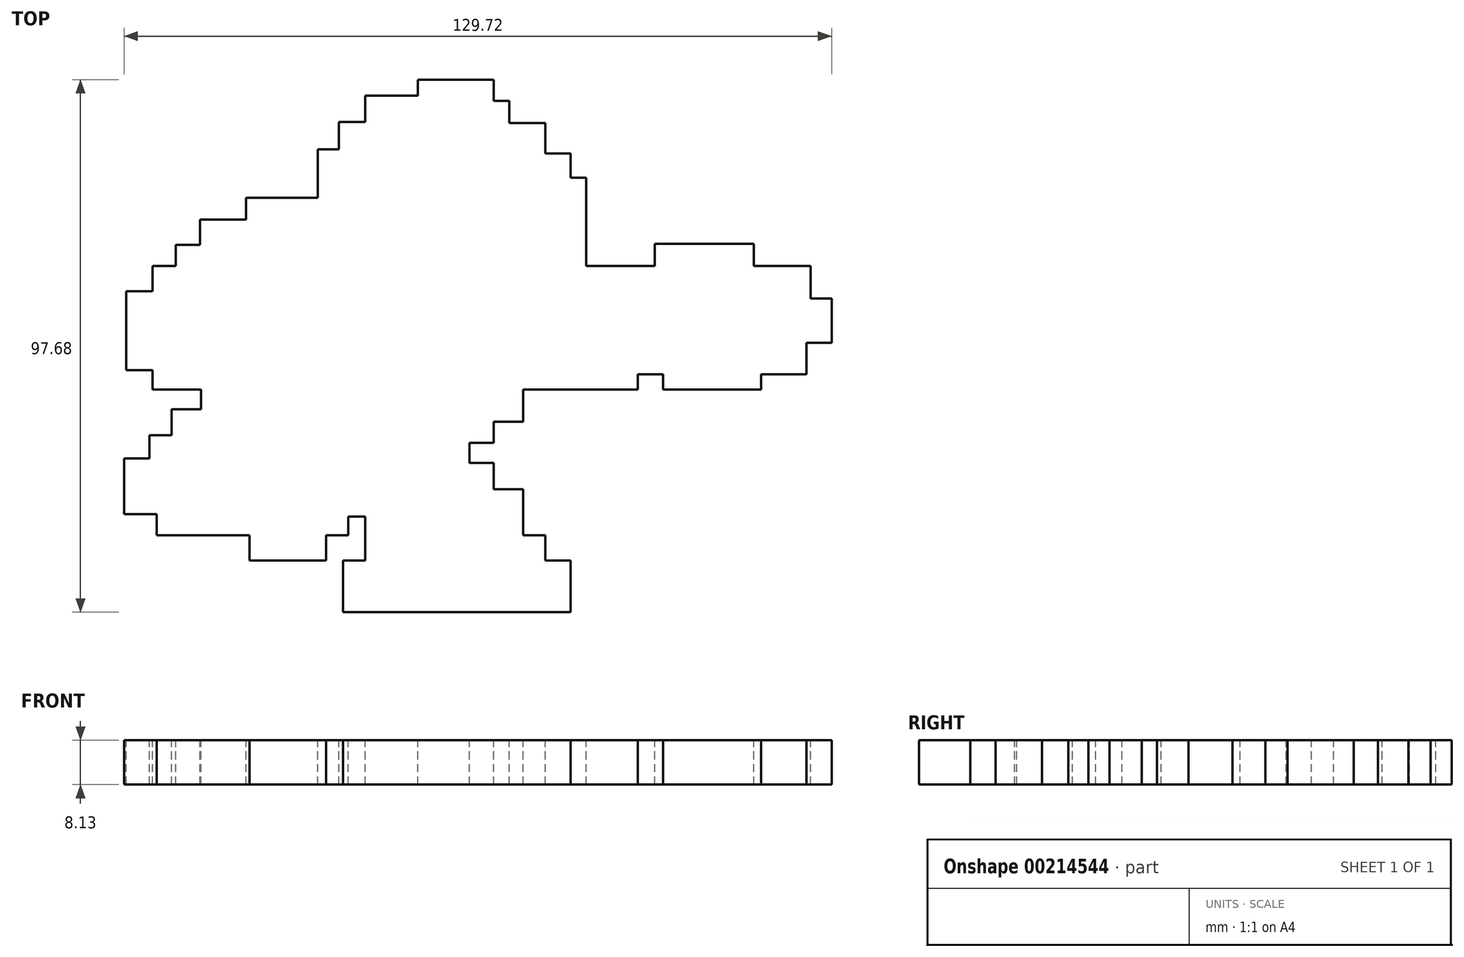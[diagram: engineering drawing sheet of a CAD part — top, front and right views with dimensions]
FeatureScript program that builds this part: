
annotation { "Feature Type Name" : "Feature", "Feature Type Description" : "" }
export const myFeature = defineFeature(function(context is Context, id is Id, definition is map)
    precondition{}
    {
        {
            var Q0;
            Q0=qCreatedBy(makeId("Top.planeOp"),FACE);
            var sketch = newSketch(context, id + "F0", { "sketchPlane" : qUnion([Q0])});
            skLineSegment(sketch, "E0", {"start": v(-13.9, 56.85) * mm, "end": v(0, 56.85) * mm});
            skLineSegment(sketch, "E1", {"start": v(0, 56.85) * mm, "end": v(0, 52.99) * mm});
            skLineSegment(sketch, "E2", {"start": v(0, 52.99) * mm, "end": v(2.9, 52.99) * mm});
            skLineSegment(sketch, "E3", {"start": v(2.9, 52.99) * mm, "end": v(2.9, 48.93) * mm});
            skLineSegment(sketch, "E4", {"start": v(2.9, 48.93) * mm, "end": v(9.47, 48.93) * mm});
            skLineSegment(sketch, "E5", {"start": v(9.47, 48.93) * mm, "end": v(9.47, 43.33) * mm});
            skLineSegment(sketch, "E6", {"start": v(9.47, 43.33) * mm, "end": v(14.1, 43.33) * mm});
            skLineSegment(sketch, "E7", {"start": v(14.1, 43.33) * mm, "end": v(14.1, 38.9) * mm});
            skLineSegment(sketch, "E8", {"start": v(14.1, 38.9) * mm, "end": v(17, 38.9) * mm});
            skLineSegment(sketch, "E9", {"start": v(17, 38.9) * mm, "end": v(17, 22.68) * mm});
            skLineSegment(sketch, "E10", {"start": v(17, 22.68) * mm, "end": v(29.54, 22.68) * mm});
            skLineSegment(sketch, "E11", {"start": v(29.54, 22.68) * mm, "end": v(29.54, 26.73) * mm});
            skLineSegment(sketch, "E12", {"start": v(29.54, 26.73) * mm, "end": v(47.69, 26.73) * mm});
            skLineSegment(sketch, "E13", {"start": v(47.69, 26.73) * mm, "end": v(47.69, 22.68) * mm});
            skLineSegment(sketch, "E14", {"start": v(47.69, 22.68) * mm, "end": v(58.1, 22.68) * mm});
            skLineSegment(sketch, "E15", {"start": v(58.1, 22.68) * mm, "end": v(58.1, 16.7) * mm});
            skLineSegment(sketch, "E16", {"start": v(58.1, 16.7) * mm, "end": v(61.97, 16.7) * mm});
            skLineSegment(sketch, "E17", {"start": v(61.97, 16.7) * mm, "end": v(61.97, 8.59) * mm});
            skLineSegment(sketch, "E18", {"start": v(61.97, 8.59) * mm, "end": v(57.34, 8.59) * mm});
            skLineSegment(sketch, "E19", {"start": v(57.34, 8.59) * mm, "end": v(57.34, 2.8) * mm});
            skLineSegment(sketch, "E20", {"start": v(57.34, 2.8) * mm, "end": v(49.04, 2.8) * mm});
            skLineSegment(sketch, "E21", {"start": v(49.04, 2.8) * mm, "end": v(49.04, 0) * mm});
            skLineSegment(sketch, "E22", {"start": v(49.04, 0) * mm, "end": v(31.09, 0) * mm});
            skLineSegment(sketch, "E23", {"start": v(31.09, 0) * mm, "end": v(31.09, 2.8) * mm});
            skLineSegment(sketch, "E24", {"start": v(31.09, 2.8) * mm, "end": v(26.45, 2.8) * mm});
            skLineSegment(sketch, "E25", {"start": v(26.45, 2.8) * mm, "end": v(26.45, 0) * mm});
            skLineSegment(sketch, "E26", {"start": v(26.45, 0) * mm, "end": v(5.41, 0) * mm});
            skLineSegment(sketch, "E27", {"start": v(5.41, 0) * mm, "end": v(5.41, -5.89) * mm});
            skLineSegment(sketch, "E28", {"start": v(5.41, -5.89) * mm, "end": v(0, -5.89) * mm});
            skLineSegment(sketch, "E29", {"start": v(0, -5.89) * mm, "end": v(0, -9.75) * mm});
            skLineSegment(sketch, "E30", {"start": v(0, -9.75) * mm, "end": v(-4.43, -9.75) * mm});
            skLineSegment(sketch, "E31", {"start": v(-4.43, -9.75) * mm, "end": v(-4.43, -13.42) * mm});
            skLineSegment(sketch, "E32", {"start": v(-4.43, -13.42) * mm, "end": v(0, -13.42) * mm});
            skLineSegment(sketch, "E33", {"start": v(0, -13.42) * mm, "end": v(0, -18.24) * mm});
            skLineSegment(sketch, "E34", {"start": v(0, -18.24) * mm, "end": v(5.41, -18.24) * mm});
            skLineSegment(sketch, "E35", {"start": v(5.41, -18.24) * mm, "end": v(5.41, -26.73) * mm});
            skLineSegment(sketch, "E36", {"start": v(5.41, -26.73) * mm, "end": v(9.47, -26.73) * mm});
            skLineSegment(sketch, "E37", {"start": v(9.47, -26.73) * mm, "end": v(9.47, -31.37) * mm});
            skLineSegment(sketch, "E38", {"start": v(9.47, -31.37) * mm, "end": v(14.1, -31.37) * mm});
            skLineSegment(sketch, "E39", {"start": v(14.1, -31.37) * mm, "end": v(14.1, -40.83) * mm});
            skLineSegment(sketch, "E40", {"start": v(14.1, -40.83) * mm, "end": v(-27.6, -40.83) * mm});
            skLineSegment(sketch, "E41", {"start": v(-27.6, -40.83) * mm, "end": v(-27.6, -31.37) * mm});
            skLineSegment(sketch, "E42", {"start": v(-27.6, -31.37) * mm, "end": v(-23.54, -31.37) * mm});
            skLineSegment(sketch, "E43", {"start": v(-23.54, -31.37) * mm, "end": v(-23.54, -23.26) * mm});
            skLineSegment(sketch, "E44", {"start": v(-23.54, -23.26) * mm, "end": v(-26.63, -23.26) * mm});
            skLineSegment(sketch, "E45", {"start": v(-26.63, -23.26) * mm, "end": v(-26.63, -26.73) * mm});
            skLineSegment(sketch, "E46", {"start": v(-26.63, -26.73) * mm, "end": v(-30.68, -26.73) * mm});
            skLineSegment(sketch, "E47", {"start": v(-30.68, -26.73) * mm, "end": v(-30.68, -31.37) * mm});
            skLineSegment(sketch, "E48", {"start": v(-30.68, -31.37) * mm, "end": v(-44.77, -31.37) * mm});
            skLineSegment(sketch, "E49", {"start": v(-44.77, -31.37) * mm, "end": v(-44.77, -26.73) * mm});
            skLineSegment(sketch, "E50", {"start": v(-44.77, -26.73) * mm, "end": v(-61.76, -26.73) * mm});
            skLineSegment(sketch, "E51", {"start": v(-61.76, -26.73) * mm, "end": v(-61.76, -22.87) * mm});
            skLineSegment(sketch, "E52", {"start": v(-61.76, -22.87) * mm, "end": v(-67.75, -22.87) * mm});
            skLineSegment(sketch, "E53", {"start": v(-67.75, -22.87) * mm, "end": v(-67.75, -12.64) * mm});
            skLineSegment(sketch, "E54", {"start": v(-67.75, -12.64) * mm, "end": v(-63.11, -12.64) * mm});
            skLineSegment(sketch, "E55", {"start": v(-63.11, -12.64) * mm, "end": v(-63.11, -8.4) * mm});
            skLineSegment(sketch, "E56", {"start": v(-63.11, -8.4) * mm, "end": v(-59.06, -8.4) * mm});
            skLineSegment(sketch, "E57", {"start": v(-59.06, -8.4) * mm, "end": v(-59.06, -3.57) * mm});
            skLineSegment(sketch, "E58", {"start": v(-59.06, -3.57) * mm, "end": v(-53.65, -3.57) * mm});
            skLineSegment(sketch, "E59", {"start": v(-53.65, -3.57) * mm, "end": v(-53.65, 0) * mm});
            skLineSegment(sketch, "E60", {"start": v(-53.65, 0) * mm, "end": v(-62.53, 0) * mm});
            skLineSegment(sketch, "E61", {"start": v(-62.53, 0) * mm, "end": v(-62.53, 3.57) * mm});
            skLineSegment(sketch, "E62", {"start": v(-62.53, 3.57) * mm, "end": v(-67.36, 3.57) * mm});
            skLineSegment(sketch, "E63", {"start": v(-67.36, 3.57) * mm, "end": v(-67.36, 18.05) * mm});
            skLineSegment(sketch, "E64", {"start": v(-67.36, 18.05) * mm, "end": v(-62.53, 18.05) * mm});
            skLineSegment(sketch, "E65", {"start": v(-62.53, 18.05) * mm, "end": v(-62.53, 22.68) * mm});
            skLineSegment(sketch, "E66", {"start": v(-62.53, 22.68) * mm, "end": v(-58.29, 22.68) * mm});
            skLineSegment(sketch, "E67", {"start": v(-58.29, 22.68) * mm, "end": v(-58.29, 26.54) * mm});
            skLineSegment(sketch, "E68", {"start": v(-58.29, 26.54) * mm, "end": v(-53.85, 26.54) * mm});
            skLineSegment(sketch, "E69", {"start": v(-53.85, 26.54) * mm, "end": v(-53.85, 31.17) * mm});
            skLineSegment(sketch, "E70", {"start": v(-53.85, 31.17) * mm, "end": v(-45.35, 31.17) * mm});
            skLineSegment(sketch, "E71", {"start": v(-45.35, 31.17) * mm, "end": v(-45.35, 35.23) * mm});
            skLineSegment(sketch, "E72", {"start": v(-45.35, 35.23) * mm, "end": v(-32.23, 35.23) * mm});
            skLineSegment(sketch, "E73", {"start": v(-32.23, 35.23) * mm, "end": v(-32.23, 44.1) * mm});
            skLineSegment(sketch, "E74", {"start": v(-32.23, 44.1) * mm, "end": v(-28.37, 44.1) * mm});
            skLineSegment(sketch, "E75", {"start": v(-28.37, 44.1) * mm, "end": v(-28.37, 49.13) * mm});
            skLineSegment(sketch, "E76", {"start": v(-28.37, 49.13) * mm, "end": v(-23.54, 49.13) * mm});
            skLineSegment(sketch, "E77", {"start": v(-23.54, 49.13) * mm, "end": v(-23.54, 53.95) * mm});
            skLineSegment(sketch, "E78", {"start": v(-23.54, 53.95) * mm, "end": v(-13.9, 53.95) * mm});
            skLineSegment(sketch, "E79", {"start": v(-13.9, 53.95) * mm, "end": v(-13.9, 56.85) * mm});
            skSolve(sketch);
        }
        {
            var Q0;
            Q0 = qSketchRegion(id + "F0", true);
            extrude(context, id + "F1", {"entities" : qUnion([Q0]), "oppositeDirection" : true, "depth" : 8.13 * mm});
        }
    });
